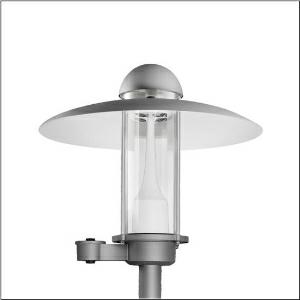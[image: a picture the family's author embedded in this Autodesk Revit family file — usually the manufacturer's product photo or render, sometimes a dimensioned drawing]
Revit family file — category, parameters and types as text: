
# Revit family: city-light_elegance___st1_2a_5xa5263et14h000032_f584
name_source: partatom
category: Lighting Fixtures
units: mm (PartAtom-declared; Revit-internal decimal feet)

## family parameters
Cut with Voids When Loaded = No
Host = Face
Light Source = No
Part Type = Normal
Room Calculation Point = No
Round Connector Dimension = Use Diameter
Shared = No

## types (1)
- --- (1 x LED, 1470 lm, 14.2 W, 3000K)
    Apparent Load = 14 VA
    CIE Flux Codes = 22 62 94 98 100
    Color Rendering = 80
    Color Temperature = 3000K
    Default Elevation = 1800 mm
    Description = City-Light Elegance, mast luminaire, Module 540 Plus, primary light control with 3 zone facetted reflector, of plastic, silver coated, highly specular, structured, primary optical cover: cover, of PMMA, transparent, light distribution: ST1.2a, light emission: direct distribution, primary light characteristic: asymmetric, installation type: post-top, LED, High Power LED, rated luminous flux: 1.470lm, luminous efficacy: 104lm/W, light colour: 730, colour temperature: 3000K, control gear: ECG Smart Interface, control: overheat protection, digital communication interface, time-dependent luminous flux control, flexible luminous flux parameterisation, presetting dimming logarithmic, with terminal, 6-pole, max. 2.5mm², mains connection: 220..240V, AC, 50/60Hz, start of lifetime: 14W, end of lifetime: 15W, reduction: 8W, luminaire housing, upper part, of aluminium, coated, Siteco® metallic grey (DB 702S), diameter: 750mm, height: 675mm, spigot size: d x l = 76 x 70mm (post-top) | with reducer (optional accessory) 60 x 70mm, post-top mast mounting element, of diecast aluminium, coated, Siteco® metallic grey (DB 702S), Module 540 Plus, traffic white (RAL 9016), protection rating (complete): IP65, insulation class (complete): insulation class II (safety insulation), certification: CE, ENEC, VDE, packaging unit: 1 piece

Light Distribution: ST1.2a
    Height = 675 mm
    Lamp = 1 x LED
    Lamp Light Flux = 1470 lm
    Lamp Power = 14.2 W
    Lamp count = 1
    Length = 750 mm
    Luminous efficacy = 104 lm/W
    Manufacturer = Siteco
    ModVariant = No
    Model = 5XA5263ET14H000032
    Number of Poles = 1
    OnlyDefault = Yes
    Power Factor = 1
    Product Name = City-Light Elegance | ST1.2a
    Product group = mast luminaire | pylon top
    ProductGroupID = 6100
    Protection Class = Protection class II
    Protection Degree = IP 65
    RLX_Detail_Level = 1
    RlxData = <blob elided: 72333 chars, md5=5454aa45>
    Socket = socket
    Standby Power = 0 W
    System Light Flux = 1470 lm
    System Power = 14 W
    Type Comments = factory setting: luminous flux: 100 % | dim-lin: 254 | 516 mA
    Type Image = l_1005991.jpg
    URL = http://relux.com
    VarID = @adj_121725
    Voltage = 0 V
    Weight = 0.00 kg
    Width = 0 mm  [stored 0 ft]

note: [stored X ft] marks values corroborated as IEEE doubles in the binary element streams (Revit-internal decimal feet)

## geometry (parser evidence)
native form markers: Blend x4, Sweep x10
no freeform markers — native parametric forms only
